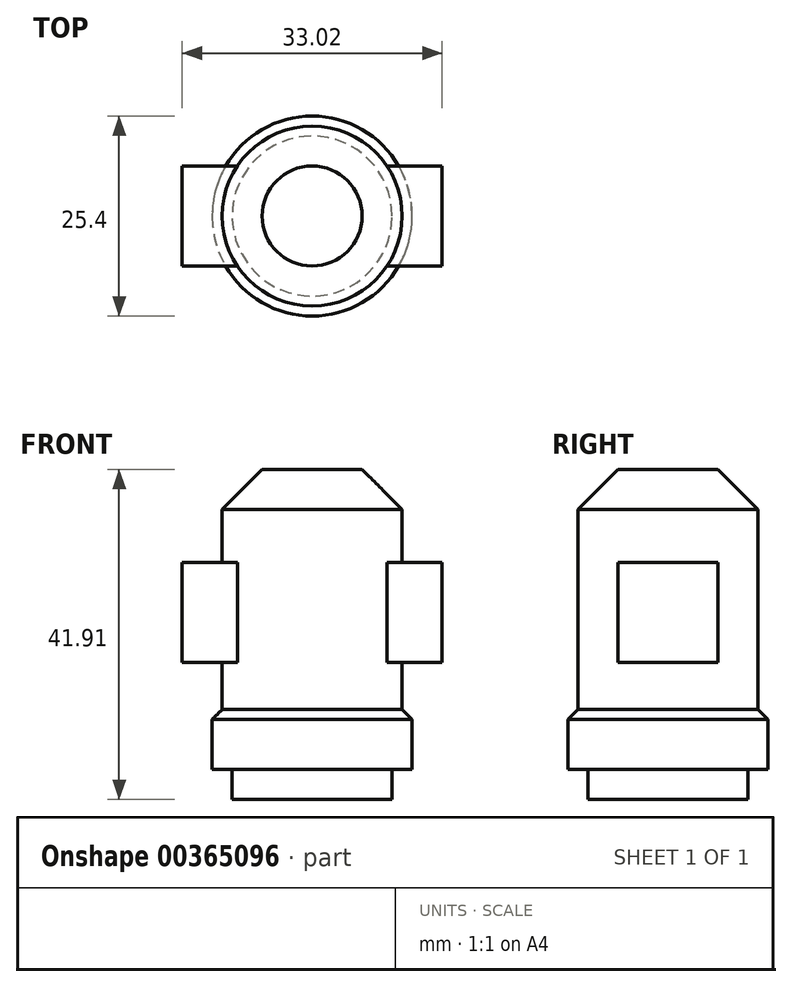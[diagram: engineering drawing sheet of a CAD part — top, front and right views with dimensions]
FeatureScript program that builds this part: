
annotation { "Feature Type Name" : "Feature", "Feature Type Description" : "" }
export const myFeature = defineFeature(function(context is Context, id is Id, definition is map)
    precondition{}
    {
        {
            var Q0;
            Q0=qCreatedBy(makeId("Top.planeOp"),FACE);
            var sketch = newSketch(context, id + "F0", { "sketchPlane" : qUnion([Q0])});
            skCircle(sketch, "E0", {"center": v(0, 0) * mm, "radius": 10.16 * mm});
            skSolve(sketch);
        }
        {
            var Q0;
            Q0=makeQuery(id+"F0.imprint","IMPRINT",FACE,{"disambiguationData":[TD([[makeQuery(id+"F0.imprint","IMPRINT",EDGE,{"derivedFrom":sQuery(id+"F0.wireOp",EDGE,"E0")}),1.0]])]});
            extrude(context, id + "F1", {"entities" : qUnion([Q0]), "oppositeDirection" : true, "depth" : 3.8 * mm});
        }
        {
            var Q0;
            Q0=qCreatedBy(makeId("Top.planeOp"),FACE);
            var sketch = newSketch(context, id + "F2", { "sketchPlane" : qUnion([Q0])});
            skCircle(sketch, "E1", {"center": v(0, 0) * mm, "radius": 12.7 * mm});
            skSolve(sketch);
        }
        {
            var Q0;
            Q0 = qSketchRegion(id + "F2", true);
            extrude(context, id + "F3", {"entities" : qUnion([Q0]), "operationType" : NewBodyOperationType.ADD, "depth" : 2.54 * mm});
        }
        {
            var Q0;
            Q0=qCreatedBy(makeId("Top.planeOp"),FACE);
            var sketch = newSketch(context, id + "F4", { "sketchPlane" : qUnion([Q0])});
            skCircle(sketch, "E2", {"center": v(0, 0) * mm, "radius": 11.43 * mm});
            skSolve(sketch);
        }
        {
            var Q0;
            Q0 = qSketchRegion(id + "F4", true);
            extrude(context, id + "F5", {"entities" : qUnion([Q0]), "operationType" : NewBodyOperationType.ADD, "depth" : 38.1 * mm});
        }
        {
            var Q0;
            Q0=makeQuery(id+"F5.opExtrude","SWEPT_FACE",FACE,{"disambiguationData":[OSD([sQuery(id+"F4.wireOp",EDGE,"E2")])]});
            chamfer(context, id + "F6", {"entities" : qUnion([Q0]), "width" : 5.08 * mm, "tangentPropagation" : true});
        }
        {
            var Q0;
            Q0=qCreatedBy(makeId("Right.planeOp"),FACE);
            var sketch = newSketch(context, id + "F7", { "sketchPlane" : qUnion([Q0])});
            skLineSegment(sketch, "E3.bottom", {"start": v(6.35, 13.61) * mm, "end": v(-6.35, 13.61) * mm});
            skLineSegment(sketch, "E3.top", {"start": v(6.35, 26.31) * mm, "end": v(-6.35, 26.31) * mm});
            skLineSegment(sketch, "E3.left", {"start": v(6.35, 13.61) * mm, "end": v(6.35, 26.31) * mm});
            skLineSegment(sketch, "E3.right", {"start": v(-6.35, 13.61) * mm, "end": v(-6.35, 26.31) * mm});
            skPoint(sketch, "E3.middle", {"position": v(0, 19.96) * mm});
            skSolve(sketch);
        }
        {
            var Q0;
            Q0 = qSketchRegion(id + "F7", true);
            extrude(context, id + "F8", {"entities" : qUnion([Q0]), "operationType" : NewBodyOperationType.ADD, "depth" : 16.5 * mm});
        }
        {
            var Q0;
            Q0=qCreatedBy(makeId("Right.planeOp"),FACE);
            var sketch = newSketch(context, id + "F9", { "sketchPlane" : qUnion([Q0])});
            skLineSegment(sketch, "E4.bottom", {"start": v(6.35, 13.61) * mm, "end": v(-6.35, 13.61) * mm});
            skLineSegment(sketch, "E4.top", {"start": v(6.35, 26.31) * mm, "end": v(-6.35, 26.31) * mm});
            skLineSegment(sketch, "E4.left", {"start": v(6.35, 13.61) * mm, "end": v(6.35, 26.31) * mm});
            skLineSegment(sketch, "E4.right", {"start": v(-6.35, 13.61) * mm, "end": v(-6.35, 26.31) * mm});
            skPoint(sketch, "E4.middle", {"position": v(0, 19.96) * mm});
            skSolve(sketch);
        }
        {
            var Q0;
            Q0 = qSketchRegion(id + "F9", true);
            extrude(context, id + "F10", {"entities" : qUnion([Q0]), "operationType" : NewBodyOperationType.ADD, "oppositeDirection" : true, "depth" : 16.5 * mm});
        }
    });
